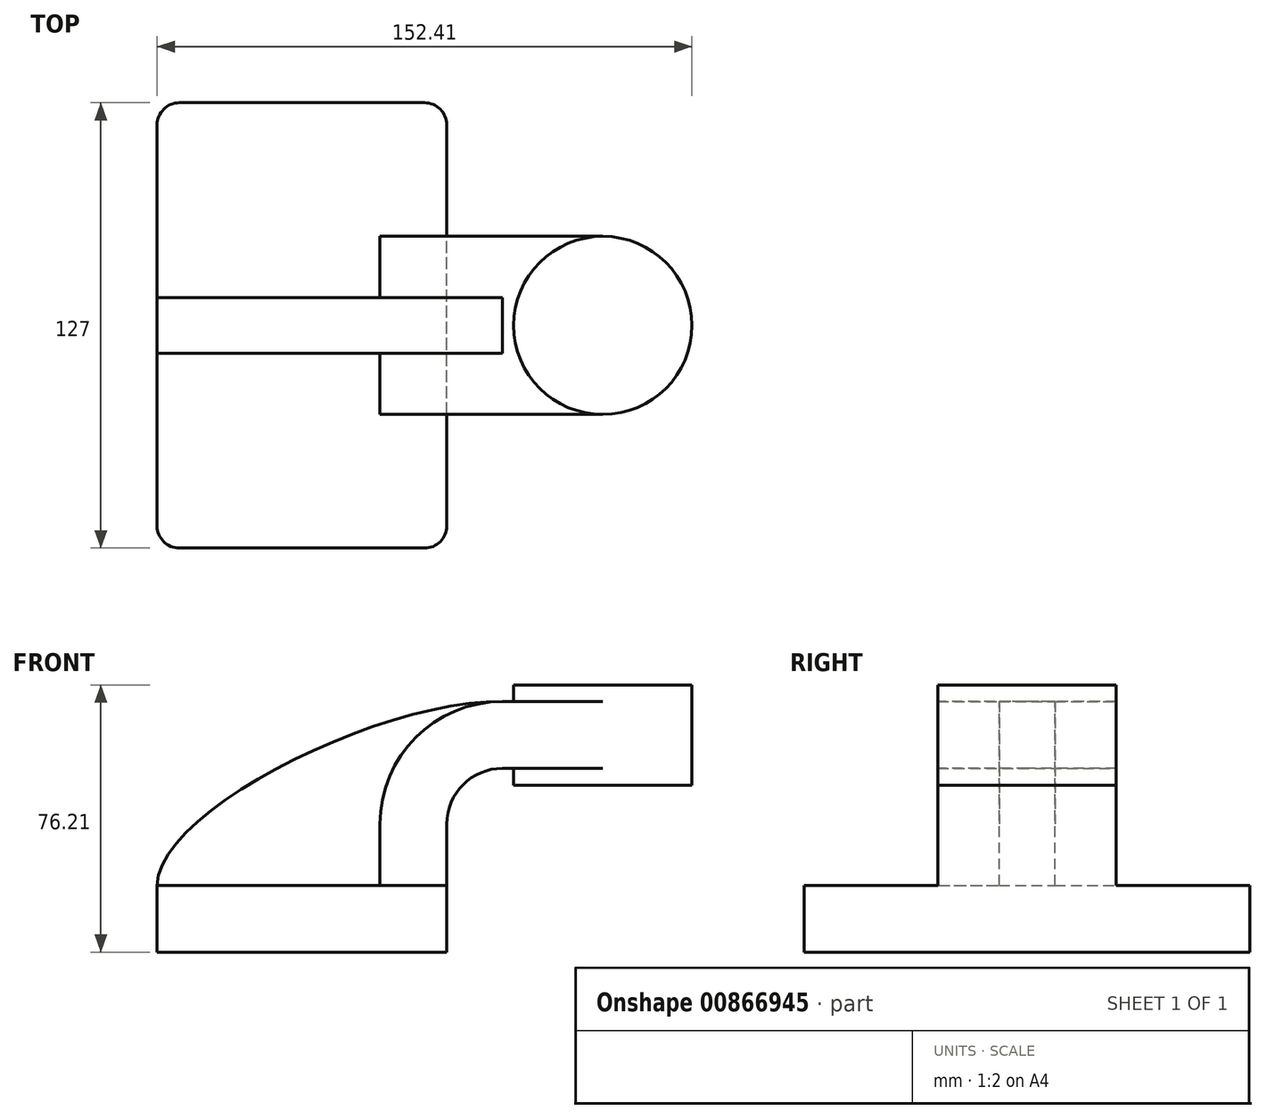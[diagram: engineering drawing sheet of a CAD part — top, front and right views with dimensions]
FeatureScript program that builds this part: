
annotation { "Feature Type Name" : "Feature", "Feature Type Description" : "" }
export const myFeature = defineFeature(function(context is Context, id is Id, definition is map)
    precondition{}
    {
        {
            var Q0;
            Q0=qCreatedBy(makeId("Front.planeOp"),FACE);
            var sketch = newSketch(context, id + "F0", { "sketchPlane" : qUnion([Q0])});
            skLineSegment(sketch, "E0.bottom", {"start": v(41.27, 9.53) * mm, "end": v(-41.28, 9.53) * mm});
            skLineSegment(sketch, "E0.top", {"start": v(41.28, -9.52) * mm, "end": v(-41.27, -9.52) * mm});
            skLineSegment(sketch, "E0.left", {"start": v(41.28, 9.53) * mm, "end": v(41.28, -9.52) * mm});
            skLineSegment(sketch, "E0.right", {"start": v(-41.28, 9.53) * mm, "end": v(-41.27, -9.52) * mm});
            skPoint(sketch, "E0.middle", {"position": v(0, 0) * mm});
            skLineSegment(sketch, "E1", {"start": v(41.27, 9.53) * mm, "end": v(41.27, 27) * mm});
            skLineSegment(sketch, "E2.bottom", {"start": v(111.12, 66.68) * mm, "end": v(60.32, 66.68) * mm});
            skLineSegment(sketch, "E2.top", {"start": v(111.12, 38.1) * mm, "end": v(60.32, 38.1) * mm});
            skLineSegment(sketch, "E2.left", {"start": v(111.12, 66.68) * mm, "end": v(111.12, 38.1) * mm});
            skLineSegment(sketch, "E2.right", {"start": v(60.32, 66.68) * mm, "end": v(60.32, 38.1) * mm});
            skPoint(sketch, "E2.middle", {"position": v(85.72, 52.39) * mm});
            skArc(sketch, "E3", {"start": v(41.27, 27) * mm, "mid": v(45.92, 38.23) * mm, "end": v(57.15, 42.88) * mm});
            skLineSegment(sketch, "E4", {"start": v(57.15, 42.88) * mm, "end": v(85.72, 42.88) * mm});
            skLineSegment(sketch, "E5.0", {"start": v(57.15, 61.93) * mm, "end": v(85.72, 61.93) * mm});
            skArc(sketch, "E5.1", {"start": v(22.23, 27) * mm, "mid": v(32.45, 51.7) * mm, "end": v(57.15, 61.93) * mm});
            skLineSegment(sketch, "E5.2", {"start": v(22.23, 9.53) * mm, "end": v(22.23, 27) * mm});
            skLineSegment(sketch, "E6", {"start": v(85.72, 38.1) * mm, "end": v(85.72, 66.68) * mm});
            skFitSpline(sketch, "E7", {"points": [v(-41.28, 9.53) * mm, v(57.15, 61.93) * mm], "startDerivative": vector(0.9, 64.54) * mm, "endDerivative": vector(103.25, -1.86) * mm});
            skSolve(sketch);
        }
        {
            var Q0;
            Q0=makeQuery(id+"F0.imprint","IMPRINT",FACE,{"disambiguationData":[TD([[makeQuery(id+"F0.imprint","IMPRINT",EDGE,{"derivedFrom":sQuery(id+"F0.wireOp",EDGE,"E0.top")}),-1.0]])]});
            extrude(context, id + "F1", {"entities" : qUnion([Q0]), "endBound" : BoundingType.SYMMETRIC, "depth" : 127 * mm, "offsetDistance" : 25.4 * mm});
        }
        {
            var Q0;
            {var subQ6=sQuery(id+"F0.wireOp",EDGE,"E1");Q0=makeQuery(id+"F0.imprint","IMPRINT",FACE,{"disambiguationData":[TD([[makeQuery(id+"F0.imprint","IMPRINT",EDGE,{"derivedFrom":subQ6}),1.0]])]});}
            var Q1;
            {var subQ0=sQuery(id+"F0.wireOp",EDGE,"E5.0");var subQ1=sQuery(id+"F0.wireOp",EDGE,"E2.right");var subQ2=makeQuery(id+"F0.imprint","INTERSECT",VERTEX,{"derivedFrom":[subQ1,subQ0]});Q1=makeQuery(id+"F0.imprint","IMPRINT",FACE,{"disambiguationData":[TD([[makeQuery(id+"F0.imprint","IMPRINT",EDGE,{"disambiguationData":[TD([[subQ2,-1.0]])],"derivedFrom":subQ1}),1.0]])]});}
            extrude(context, id + "F2", {"entities" : qUnion([Q0, Q1]), "operationType" : NewBodyOperationType.ADD, "endBound" : BoundingType.SYMMETRIC, "depth" : 50.8 * mm, "offsetDistance" : 25.4 * mm});
        }
        {
            var Q0;
            {var subQ3=sQuery(id+"F0.wireOp",EDGE,"E5.2");Q0=makeQuery(id+"F0.imprint","IMPRINT",FACE,{"disambiguationData":[TD([[makeQuery(id+"F0.imprint","IMPRINT",EDGE,{"derivedFrom":subQ3}),1.0]])]});}
            extrude(context, id + "F3", {"entities" : qUnion([Q0]), "operationType" : NewBodyOperationType.ADD, "endBound" : BoundingType.SYMMETRIC, "depth" : 15.88 * mm, "offsetDistance" : 25.4 * mm});
        }
        {
            var Q0;
            {var subQ0=sQuery(id+"F0.wireOp",EDGE,"E2.left");Q0=makeQuery(id+"F0.imprint","IMPRINT",FACE,{"disambiguationData":[TD([[makeQuery(id+"F0.imprint","IMPRINT",EDGE,{"derivedFrom":subQ0}),-1.0]])]});}
            var Q1;
            Q1=sQuery(id+"F0.wireOp",EDGE,"E6");
            revolve(context, id + "F4", {"operationType" : NewBodyOperationType.ADD, "surfaceOperationType" : NewSurfaceOperationType.NEW, "entities" : qUnion([Q0]), "axis" : qUnion([Q1]), "revolveType" : RevolveType.FULL});
        }
        {
            var Q0;
            Q0=makeQuery(id+"F1.opExtrude","CAP_EDGE",EDGE,{"disambiguationData":[OSD([sQuery(id+"F0.wireOp",EDGE,"E0.left")])],"isStart":false});
            var Q1;
            Q1=makeQuery(id+"F1.opExtrude","CAP_EDGE",EDGE,{"disambiguationData":[OSD([sQuery(id+"F0.wireOp",EDGE,"E0.right")])],"isStart":false});
            var Q2;
            Q2=makeQuery(id+"F1.opExtrude","CAP_EDGE",EDGE,{"disambiguationData":[OSD([sQuery(id+"F0.wireOp",EDGE,"E0.left")])],"isStart":true});
            var Q3;
            Q3=makeQuery(id+"F1.opExtrude","CAP_EDGE",EDGE,{"disambiguationData":[OSD([sQuery(id+"F0.wireOp",EDGE,"E0.right")])],"isStart":true});
            fillet(context, id + "F5", {"entities" : qUnion([Q0, Q1, Q2, Q3]), "radius" : 6.35 * mm, "tangentPropagation" : true, "allowEdgeOverflow" : false});
        }
    });
